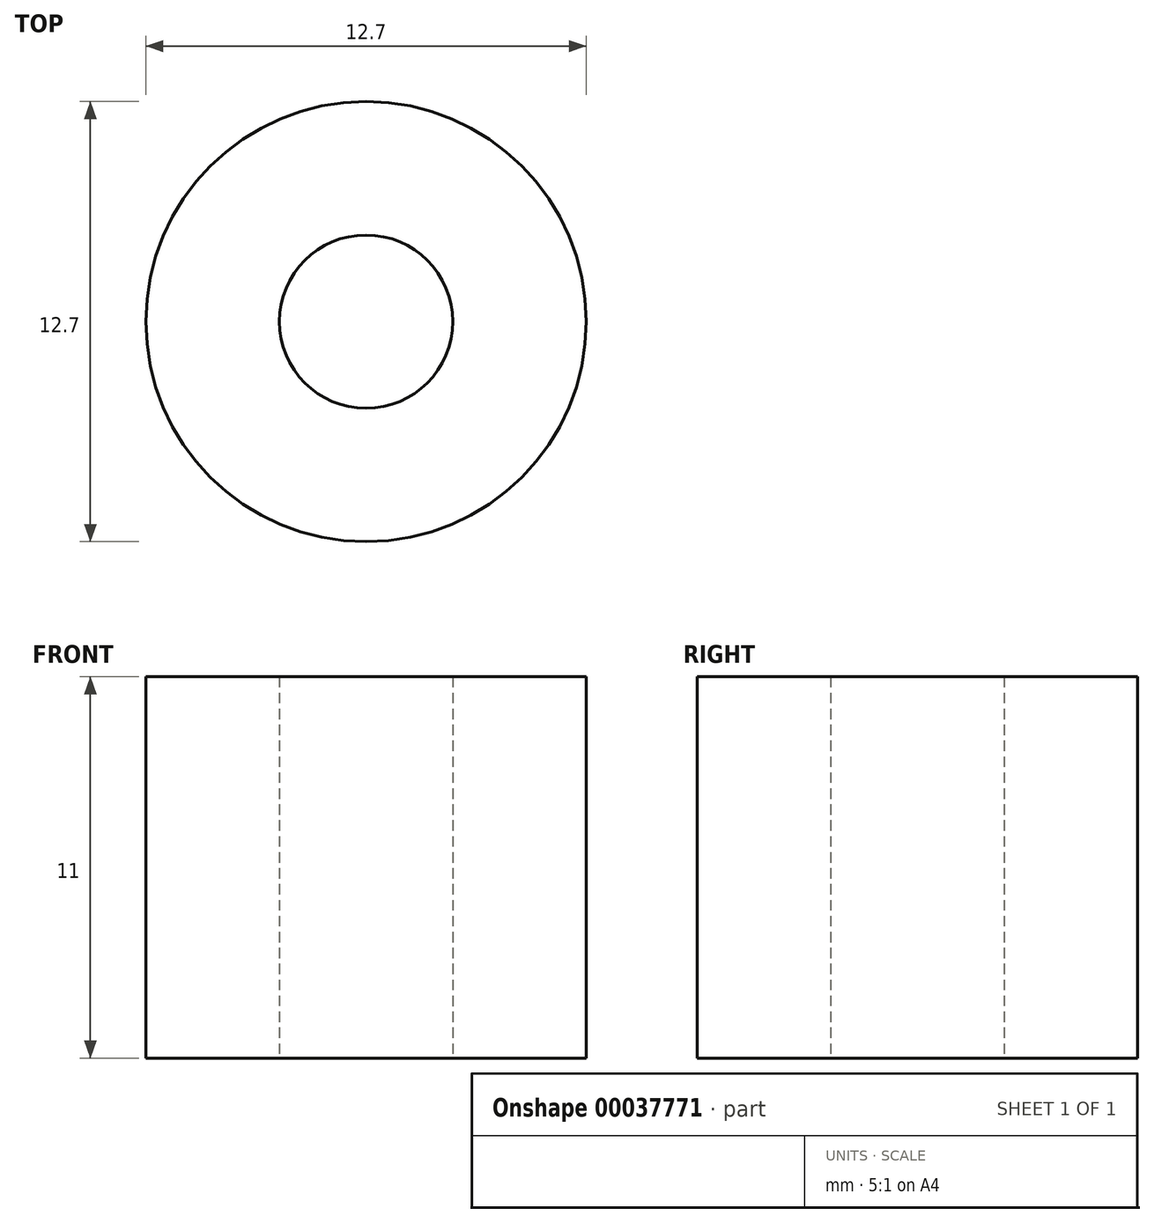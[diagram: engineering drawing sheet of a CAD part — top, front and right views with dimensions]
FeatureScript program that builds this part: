
annotation { "Feature Type Name" : "Feature", "Feature Type Description" : "" }
export const myFeature = defineFeature(function(context is Context, id is Id, definition is map)
    precondition{}
    {
        {
            var Q0;
            Q0=qCreatedBy(makeId("Top.planeOp"),FACE);
            var sketch = newSketch(context, id + "F0", { "sketchPlane" : qUnion([Q0])});
            skCircle(sketch, "E0", {"center": v(0, 0) * mm, "radius": 6.35 * mm});
            skCircle(sketch, "E1", {"center": v(0, 0) * mm, "radius": 2.5 * mm});
            skSolve(sketch);
        }
        {
            var Q0;
            Q0 = qSketchRegion(id + "F0", true);
            extrude(context, id + "F1", {"entities" : qUnion([Q0]), "depth" : 11 * mm});
        }
    });
